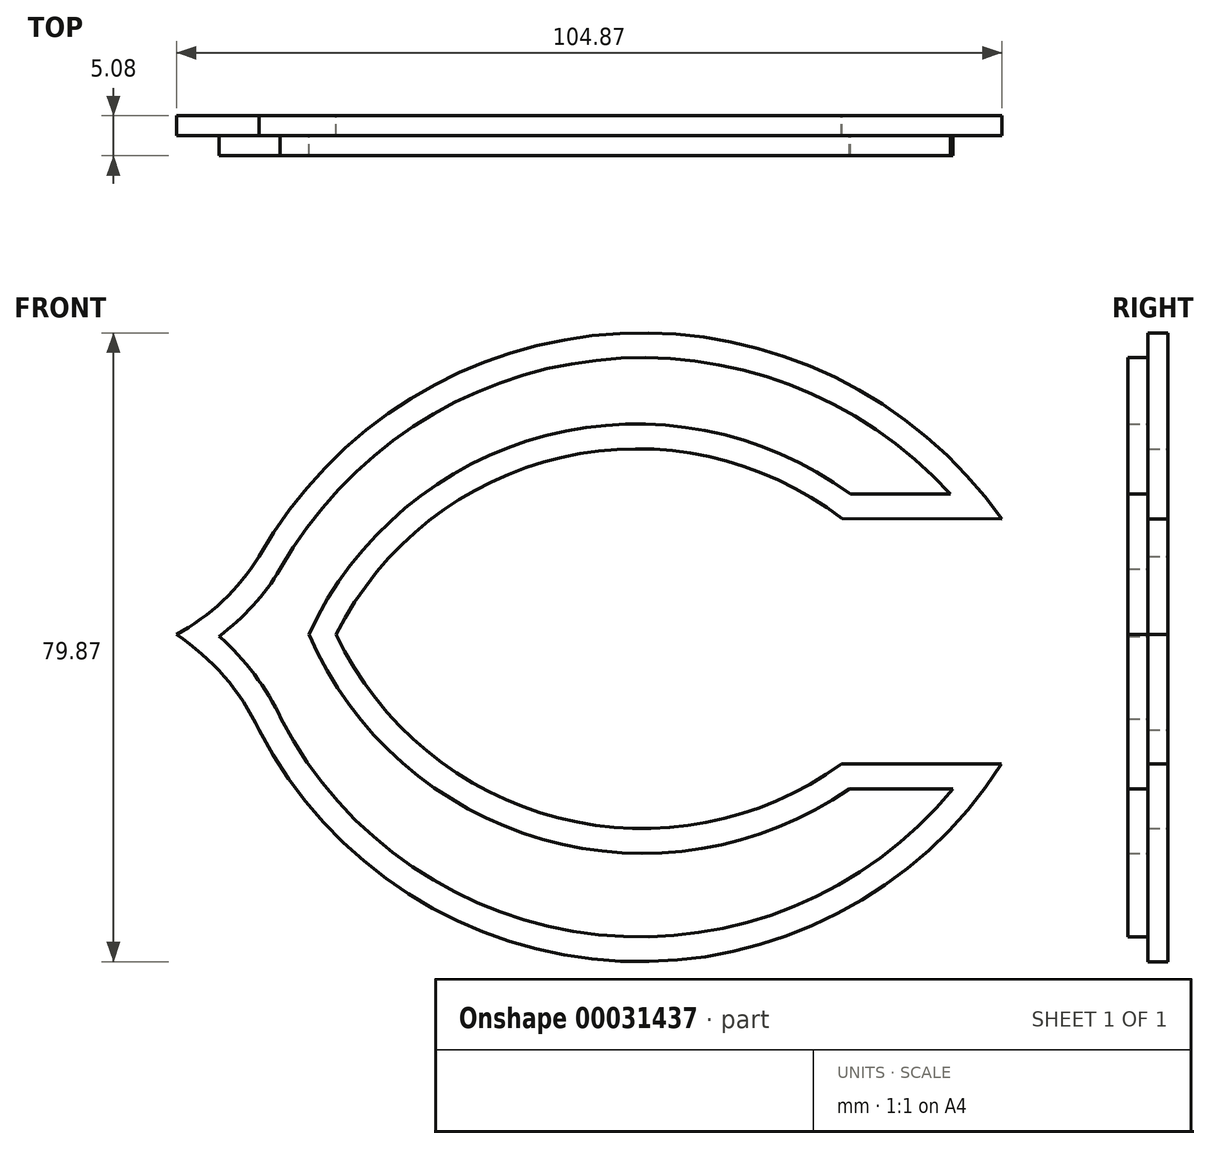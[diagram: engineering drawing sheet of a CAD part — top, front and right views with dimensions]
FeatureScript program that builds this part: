
annotation { "Feature Type Name" : "Feature", "Feature Type Description" : "" }
export const myFeature = defineFeature(function(context is Context, id is Id, definition is map)
    precondition{}
    {
        {
            var Q0;
            Q0=qCreatedBy(makeId("Front.planeOp"),FACE);
            var sketch = newSketch(context, id + "F0", { "sketchPlane" : qUnion([Q0])});
            skArc(sketch, "E0", {"start": v(-100.34, 4.92) * mm, "mid": v(-94.44, 9.19) * mm, "end": v(-89.85, 14.84) * mm});
            skPoint(sketch, "E1.end.orphan", {"position": v(-89.85, -29.27) * mm});
            skArc(sketch, "E2", {"start": v(-89.85, -7.21) * mm, "mid": v(-43.92, -36.58) * mm, "end": v(4.5, -11.53) * mm});
            skLineSegment(sketch, "E3", {"start": v(4.5, -11.53) * mm, "end": v(-15.83, -11.53) * mm});
            skArc(sketch, "E4", {"start": v(4.53, 19.6) * mm, "mid": v(-43.97, 43.16) * mm, "end": v(-89.85, 14.84) * mm});
            skLineSegment(sketch, "E5", {"start": v(-15.79, 19.63) * mm, "end": v(4.53, 19.6) * mm});
            skPoint(sketch, "E6.endSnap0", {"position": v(-11.7, 4.73) * mm});
            skArc(sketch, "E7", {"start": v(-15.79, 19.63) * mm, "mid": v(-51.38, 27.43) * mm, "end": v(-80.03, 4.9) * mm});
            skArc(sketch, "E8", {"start": v(-80.03, 4.9) * mm, "mid": v(-51.79, -18.38) * mm, "end": v(-15.83, -11.53) * mm});
            skLineSegment(sketch, "E9", {"start": v(-100.34, 4.92) * mm, "end": v(-80.03, 4.9) * mm});
            skArc(sketch, "E10", {"start": v(-89.85, -7.21) * mm, "mid": v(-94.26, -0.42) * mm, "end": v(-100.34, 4.92) * mm});
            skLineSegment(sketch, "E11.0", {"start": v(-14.77, 22.68) * mm, "end": v(-1.82, 22.67) * mm});
            skArc(sketch, "E11.1", {"start": v(-1.82, 22.67) * mm, "mid": v(-46.92, 39.86) * mm, "end": v(-87.22, 13.3) * mm});
            skArc(sketch, "E11.2", {"start": v(-95.04, 4.7) * mm, "mid": v(-90.72, 8.62) * mm, "end": v(-87.22, 13.3) * mm});
            skArc(sketch, "E11.3", {"start": v(-87.1, -5.86) * mm, "mid": v(-90.53, -0.18) * mm, "end": v(-95.04, 4.7) * mm});
            skArc(sketch, "E11.4", {"start": v(-87.1, -5.86) * mm, "mid": v(-46.65, -33.32) * mm, "end": v(-1.48, -14.58) * mm});
            skArc(sketch, "E11.5", {"start": v(-14.77, 22.68) * mm, "mid": v(-53.3, 30.1) * mm, "end": v(-83.4, 4.94) * mm});
            skLineSegment(sketch, "E11.6", {"start": v(-1.48, -14.58) * mm, "end": v(-14.86, -14.58) * mm});
            skArc(sketch, "E11.7", {"start": v(-83.4, 4.94) * mm, "mid": v(-53.74, -21.02) * mm, "end": v(-14.86, -14.58) * mm});
            skSolve(sketch);
        }
        {
            var Q0;
            {var subQ8=sQuery(id+"F0.wireOp",EDGE,"E0");Q0=makeQuery(id+"F0.imprint","IMPRINT",FACE,{"disambiguationData":[TD([[makeQuery(id+"F0.imprint","IMPRINT",EDGE,{"derivedFrom":subQ8}),-1.0]])]});}
            var Q1;
            Q1=makeQuery(id+"F0.imprint","IMPRINT",FACE,{"disambiguationData":[TD([[makeQuery(id+"F0.imprint","IMPRINT",EDGE,{"derivedFrom":sQuery(id+"F0.wireOp",EDGE,"E11.0")}),1.0]])]});
            var Q2;
            {var subQ6=sQuery(id+"F0.wireOp",EDGE,"E11.3");Q2=makeQuery(id+"F0.imprint","IMPRINT",FACE,{"disambiguationData":[TD([[makeQuery(id+"F0.imprint","IMPRINT",EDGE,{"derivedFrom":subQ6}),-1.0]])]});}
            var Q3;
            Q3=makeQuery(id+"F0.imprint","IMPRINT",FACE,{"disambiguationData":[TD([[makeQuery(id+"F0.imprint","IMPRINT",EDGE,{"derivedFrom":sQuery(id+"F0.wireOp",EDGE,"E2")}),1.0]])]});
            extrude(context, id + "F1", {"entities" : qUnion([Q0, Q1, Q2, Q3]), "depth" : 2.54 * mm});
        }
        {
            var Q0;
            Q0=makeQuery(id+"F1.opExtrude","CAP_FACE",FACE,{"disambiguationData":[OSD([sQuery(id+"F0.wireOp",EDGE,"E0"),sQuery(id+"F0.wireOp",EDGE,"E2"),sQuery(id+"F0.wireOp",EDGE,"E3"),sQuery(id+"F0.wireOp",EDGE,"E4"),sQuery(id+"F0.wireOp",EDGE,"E5"),sQuery(id+"F0.wireOp",EDGE,"E7"),sQuery(id+"F0.wireOp",EDGE,"E8"),sQuery(id+"F0.wireOp",EDGE,"E10")])],"isStart":false});
            var sketch = newSketch(context, id + "F2", { "sketchPlane" : qUnion([Q0])});
            skArc(sketch, "E12.0", {"start": v(-2.03, 22.76) * mm, "mid": v(-47.02, 39.76) * mm, "end": v(-87.13, 13.24) * mm});
            skLineSegment(sketch, "E12.1", {"start": v(-14.73, 22.78) * mm, "end": v(-2.03, 22.76) * mm});
            skArc(sketch, "E12.2", {"start": v(-83.5, 4.94) * mm, "mid": v(-53.35, 30.2) * mm, "end": v(-14.73, 22.78) * mm});
            skArc(sketch, "E12.3", {"start": v(-14.83, -14.68) * mm, "mid": v(-53.8, -21.1) * mm, "end": v(-83.5, 4.94) * mm});
            skLineSegment(sketch, "E12.4", {"start": v(-1.68, -14.68) * mm, "end": v(-14.83, -14.68) * mm});
            skArc(sketch, "E12.5", {"start": v(-87.13, 13.24) * mm, "mid": v(-90.6, 8.6) * mm, "end": v(-94.89, 4.7) * mm});
            skArc(sketch, "E12.6", {"start": v(-87.02, -5.82) * mm, "mid": v(-46.74, -33.22) * mm, "end": v(-1.68, -14.68) * mm});
            skArc(sketch, "E12.7", {"start": v(-94.89, 4.7) * mm, "mid": v(-90.42, -0.17) * mm, "end": v(-87.02, -5.82) * mm});
            skSolve(sketch);
        }
        {
            var Q0;
            Q0=makeQuery(id+"F2.imprint","IMPRINT",FACE,{"disambiguationData":[TD([[makeQuery(id+"F2.imprint","IMPRINT",EDGE,{"derivedFrom":sQuery(id+"F2.wireOp",EDGE,"E12.0")}),1.0]])]});
            extrude(context, id + "F3", {"entities" : qUnion([Q0]), "operationType" : NewBodyOperationType.ADD, "depth" : 2.54 * mm});
        }
    });
